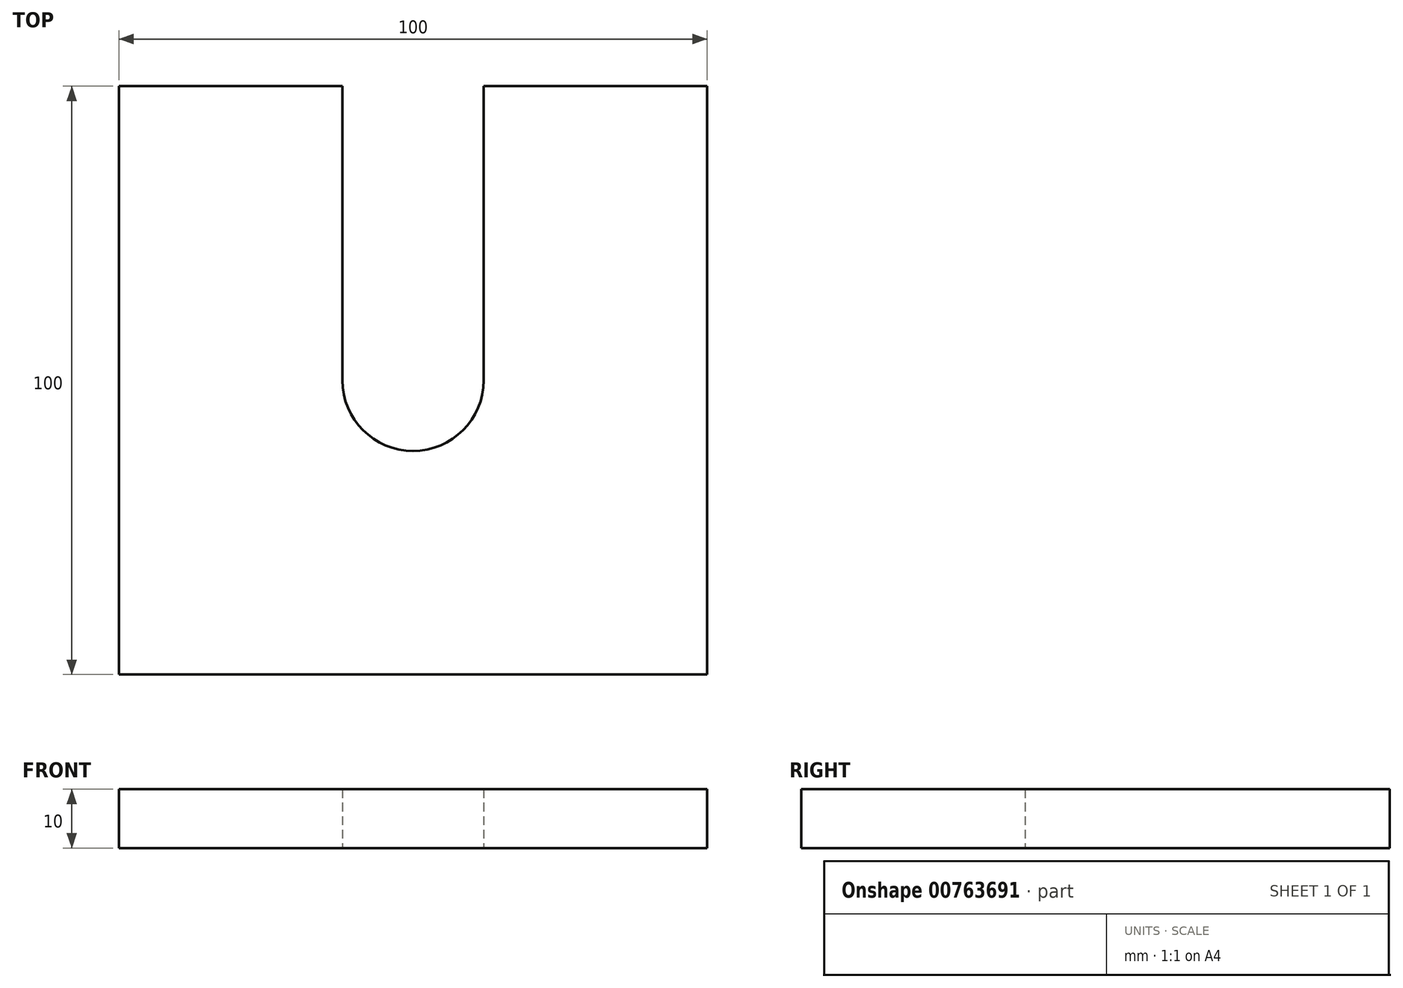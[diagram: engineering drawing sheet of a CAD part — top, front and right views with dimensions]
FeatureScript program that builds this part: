
annotation { "Feature Type Name" : "Feature", "Feature Type Description" : "" }
export const myFeature = defineFeature(function(context is Context, id is Id, definition is map)
    precondition{}
    {
        {
            var Q0;
            Q0=qCreatedBy(makeId("Top.planeOp"),FACE);
            var sketch = newSketch(context, id + "F0", { "sketchPlane" : qUnion([Q0])});
            skLineSegment(sketch, "E0.bottom", {"start": v(-50, 50) * mm, "end": v(50, 50) * mm});
            skLineSegment(sketch, "E0.top", {"start": v(-50, -50) * mm, "end": v(50, -50) * mm});
            skLineSegment(sketch, "E0.left", {"start": v(-50, 50) * mm, "end": v(-50, -50) * mm});
            skLineSegment(sketch, "E0.right", {"start": v(50, 50) * mm, "end": v(50, -50) * mm});
            skCircle(sketch, "E1", {"center": v(0, 0) * mm, "radius": 12 * mm});
            skLineSegment(sketch, "E2", {"start": v(-12, 0) * mm, "end": v(-12, 50) * mm});
            skLineSegment(sketch, "E3", {"start": v(12, 0) * mm, "end": v(12, 50) * mm});
            skSolve(sketch);
        }
        {
            var Q0;
            Q0=makeQuery(id+"F0.imprint","IMPRINT",FACE,{"disambiguationData":[TD([[makeQuery(id+"F0.imprint","IMPRINT",EDGE,{"derivedFrom":sQuery(id+"F0.wireOp",EDGE,"E0.bottom")}),-1.0]])]});
            extrude(context, id + "F1", {"entities" : qUnion([Q0]), "depth" : 10 * mm, "offsetDistance" : 25.4 * mm});
        }
    });
